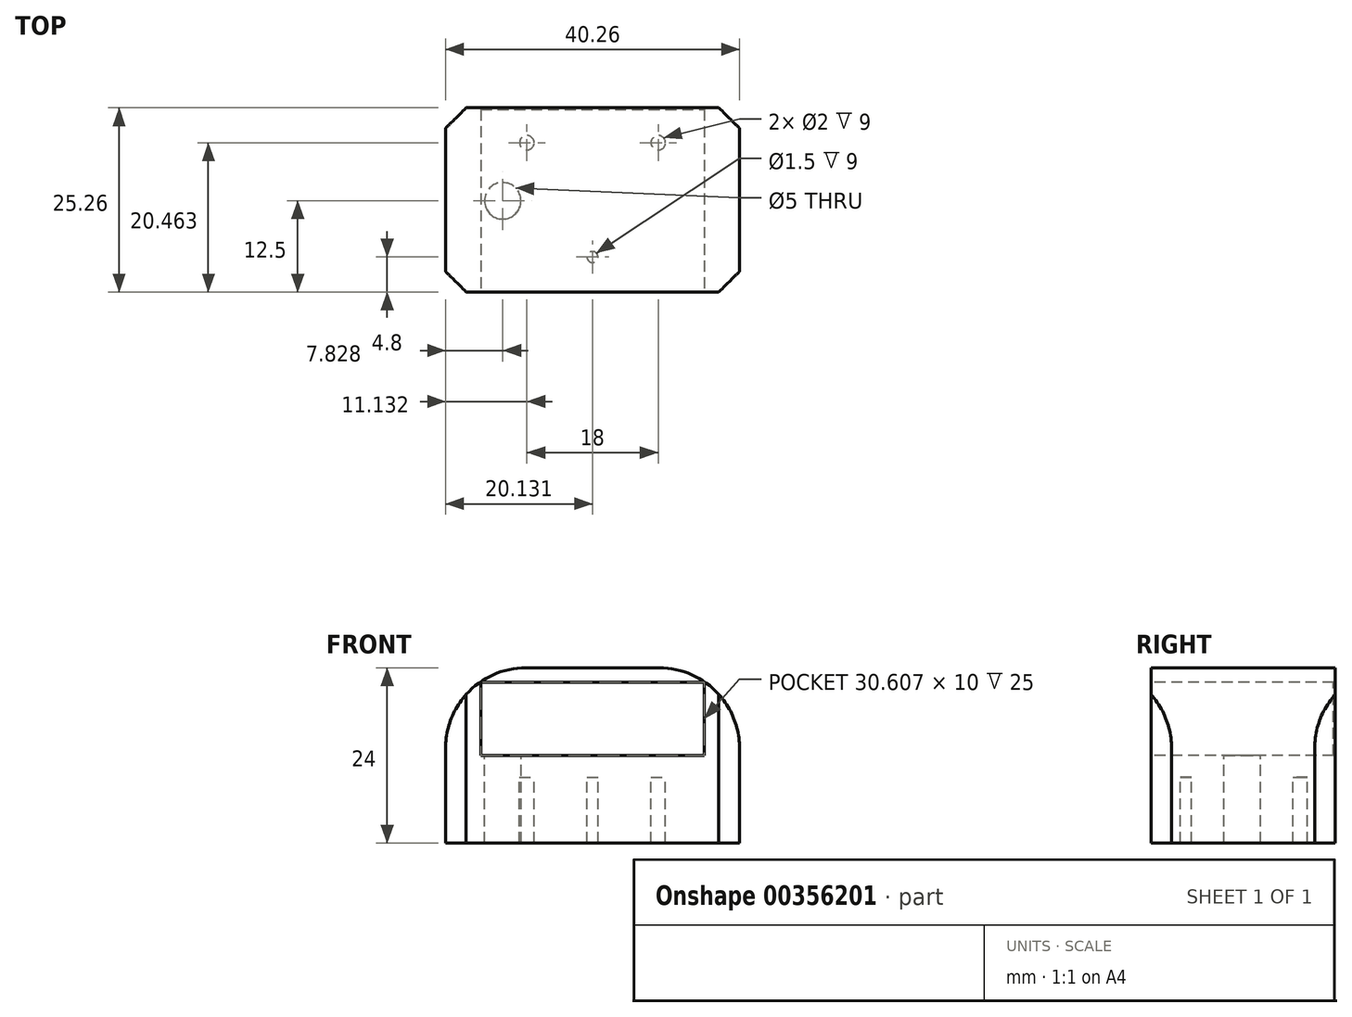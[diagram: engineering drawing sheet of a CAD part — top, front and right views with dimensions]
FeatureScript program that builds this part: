
annotation { "Feature Type Name" : "Feature", "Feature Type Description" : "" }
export const myFeature = defineFeature(function(context is Context, id is Id, definition is map)
    precondition{}
    {
        {
            var Q0;
            Q0=qCreatedBy(makeId("Top.planeOp"),FACE);
            var sketch = newSketch(context, id + "F0", { "sketchPlane" : qUnion([Q0])});
            skPoint(sketch, "E0", {"position": v(2.83, 25.26) * mm});
            skPoint(sketch, "E1", {"position": v(0, 22.43) * mm});
            skPoint(sketch, "E2", {"position": v(0, 2.83) * mm});
            skPoint(sketch, "E3", {"position": v(2.83, 0) * mm});
            skPoint(sketch, "E4", {"position": v(37.44, 0) * mm});
            skPoint(sketch, "E5", {"position": v(40.26, 2.83) * mm});
            skPoint(sketch, "E6", {"position": v(40.26, 22.43) * mm});
            skPoint(sketch, "E7", {"position": v(37.44, 25.26) * mm});
            skLineSegment(sketch, "E8", {"start": v(2.83, 25.26) * mm, "end": v(37.44, 25.26) * mm});
            skLineSegment(sketch, "E9", {"start": v(40.26, 22.43) * mm, "end": v(37.44, 25.26) * mm});
            skLineSegment(sketch, "E10", {"start": v(2.83, 25.26) * mm, "end": v(0, 22.43) * mm});
            skLineSegment(sketch, "E11", {"start": v(0, 22.43) * mm, "end": v(0, 2.83) * mm});
            skLineSegment(sketch, "E12", {"start": v(2.83, 0) * mm, "end": v(0, 2.83) * mm});
            skLineSegment(sketch, "E13", {"start": v(2.83, 0) * mm, "end": v(37.44, 0) * mm});
            skLineSegment(sketch, "E14", {"start": v(40.26, 2.83) * mm, "end": v(37.44, 0) * mm});
            skLineSegment(sketch, "E15", {"start": v(40.26, 2.83) * mm, "end": v(40.26, 22.43) * mm});
            skSolve(sketch);
        }
        {
            var Q0;
            Q0=qSketchRegion(id+"F0",true);
            extrude(context, id + "F1", {"entities" : qUnion([Q0]), "depth" : 15 * mm, "offsetDistance" : 25 * mm});
        }
        {
            var Q0;
            Q0=makeQuery(id+"F1.opExtrude","SWEPT_FACE",FACE,{"disambiguationData":[OSD([sQuery(id+"F0.wireOp",EDGE,"E13")])]});
            var sketch = newSketch(context, id + "F2", { "sketchPlane" : qUnion([Q0])});
            skPoint(sketch, "E16", {"position": v(4.83, 0) * mm});
            skPoint(sketch, "E17", {"position": v(2.83, 3) * mm});
            skPoint(sketch, "E18", {"position": v(35.44, 0) * mm});
            skPoint(sketch, "E19", {"position": v(37.44, 3) * mm});
            skLineSegment(sketch, "E20.bottom", {"start": v(4.83, 3) * mm, "end": v(35.44, 3) * mm});
            skLineSegment(sketch, "E20.top", {"start": v(4.83, 13) * mm, "end": v(35.44, 13) * mm});
            skLineSegment(sketch, "E20.left", {"start": v(4.83, 3) * mm, "end": v(4.83, 13) * mm});
            skLineSegment(sketch, "E20.right", {"start": v(35.44, 3) * mm, "end": v(35.44, 13) * mm});
            skSolve(sketch);
        }
        {
            var Q0;
            Q0=qSketchRegion(id+"F2",true);
            extrude(context, id + "F3", {"entities" : qUnion([Q0]), "operationType" : NewBodyOperationType.REMOVE, "oppositeDirection" : true, "depth" : 25 * mm});
        }
        {
            var Q0;
            Q0=qSketchRegion(id+"F2",true);
            extrude(context, id + "F4", {"entities" : qUnion([Q0]), "operationType" : NewBodyOperationType.REMOVE, "oppositeDirection" : true, "depth" : 20 * mm});
        }
        {
            var Q0;
            Q0=makeQuery(id+"F1.opExtrude","CAP_FACE",FACE,{"disambiguationData":[OSD([sQuery(id+"F0.wireOp",EDGE,"E8"),sQuery(id+"F0.wireOp",EDGE,"E9"),sQuery(id+"F0.wireOp",EDGE,"E10"),sQuery(id+"F0.wireOp",EDGE,"E11"),sQuery(id+"F0.wireOp",EDGE,"E12"),sQuery(id+"F0.wireOp",EDGE,"E13"),sQuery(id+"F0.wireOp",EDGE,"E14"),sQuery(id+"F0.wireOp",EDGE,"E15")])],"isStart":true});
            var sketch = newSketch(context, id + "F5", { "sketchPlane" : qUnion([Q0])});
            skPoint(sketch, "E21", {"position": v(0, -4.8) * mm});
            skPoint(sketch, "E22", {"position": v(0, -20.46) * mm});
            skPoint(sketch, "E23", {"position": v(40.26, -20.46) * mm});
            skPoint(sketch, "E24", {"position": v(40.26, -4.8) * mm});
            skLineSegment(sketch, "E25", {"start": v(40.26, -4.8) * mm, "end": v(0, -4.8) * mm});
            skLineSegment(sketch, "E26", {"start": v(0, -20.46) * mm, "end": v(40.26, -20.46) * mm});
            skCircle(sketch, "E27", {"center": v(20.13, -20.46) * mm, "radius": 1.5 * mm});
            skCircle(sketch, "E28", {"center": v(20.13, -4.8) * mm, "radius": 0.75 * mm});
            skPoint(sketch, "E29", {"position": v(11.13, -20.46) * mm});
            skPoint(sketch, "E30", {"position": v(29.13, -20.46) * mm});
            skCircle(sketch, "E31", {"center": v(29.13, -20.46) * mm, "radius": 1 * mm});
            skCircle(sketch, "E32", {"center": v(11.13, -20.46) * mm, "radius": 1 * mm});
            skPoint(sketch, "E33", {"position": v(29.13, -4.8) * mm});
            skSolve(sketch);
        }
        {
            var Q0;
            {var subQ0=sQuery(id+"F5.wireOp",EDGE,"Hm4tZGDY-VvXF-VA69-rOPO-ANf0YDS5IOW7");var subQ1=sQuery(id+"F5.wireOp",EDGE,"E25");var subQ2=makeQuery(id+"F5.imprint","INTERSECT",VERTEX,{"disambiguationData":[OD(0.0)],"derivedFrom":[subQ1,subQ0]});Q0=makeQuery(id+"F5.imprint","IMPRINT",FACE,{"disambiguationData":[TD([[makeQuery(id+"F5.imprint","IMPRINT",EDGE,{"disambiguationData":[TD([[subQ2,-1.0]])],"derivedFrom":subQ1}),-1.0]])]});}
            var Q1;
            {var subQ0=sQuery(id+"F5.wireOp",EDGE,"Hm4tZGDY-VvXF-VA69-rOPO-ANf0YDS5IOW7");var subQ1=sQuery(id+"F5.wireOp",EDGE,"E25");var subQ2=makeQuery(id+"F5.imprint","INTERSECT",VERTEX,{"disambiguationData":[OD(0.0)],"derivedFrom":[subQ1,subQ0]});Q1=makeQuery(id+"F5.imprint","IMPRINT",FACE,{"disambiguationData":[TD([[makeQuery(id+"F5.imprint","IMPRINT",EDGE,{"disambiguationData":[TD([[subQ2,-1.0]])],"derivedFrom":subQ1}),1.0]])]});}
            var Q2;
            {var subQ0=sQuery(id+"F5.wireOp",EDGE,"zMm4eNvp-IzTt-C4ok-0BIf-annPHVDxMdSz");var subQ1=sQuery(id+"F5.wireOp",EDGE,"E25");var subQ2=makeQuery(id+"F5.imprint","INTERSECT",VERTEX,{"disambiguationData":[OD(0.0)],"derivedFrom":[subQ1,subQ0]});Q2=makeQuery(id+"F5.imprint","IMPRINT",FACE,{"disambiguationData":[TD([[makeQuery(id+"F5.imprint","IMPRINT",EDGE,{"disambiguationData":[TD([[subQ2,-1.0]])],"derivedFrom":subQ1}),-1.0]])]});}
            var Q3;
            {var subQ0=sQuery(id+"F5.wireOp",EDGE,"zMm4eNvp-IzTt-C4ok-0BIf-annPHVDxMdSz");var subQ1=sQuery(id+"F5.wireOp",EDGE,"E25");var subQ2=makeQuery(id+"F5.imprint","INTERSECT",VERTEX,{"disambiguationData":[OD(0.0)],"derivedFrom":[subQ1,subQ0]});Q3=makeQuery(id+"F5.imprint","IMPRINT",FACE,{"disambiguationData":[TD([[makeQuery(id+"F5.imprint","IMPRINT",EDGE,{"disambiguationData":[TD([[subQ2,-1.0]])],"derivedFrom":subQ1}),1.0]])]});}
            var Q4;
            {var subQ0=sQuery(id+"F5.wireOp",EDGE,"E32");var subQ1=sQuery(id+"F5.wireOp",EDGE,"E26");var subQ2=makeQuery(id+"F5.imprint","INTERSECT",VERTEX,{"disambiguationData":[OD(0.0)],"derivedFrom":[subQ1,subQ0]});Q4=makeQuery(id+"F5.imprint","IMPRINT",FACE,{"disambiguationData":[TD([[makeQuery(id+"F5.imprint","IMPRINT",EDGE,{"disambiguationData":[TD([[subQ2,-1.0]])],"derivedFrom":subQ1}),1.0]])]});}
            var Q5;
            {var subQ0=sQuery(id+"F5.wireOp",EDGE,"E32");var subQ1=sQuery(id+"F5.wireOp",EDGE,"E26");var subQ2=makeQuery(id+"F5.imprint","INTERSECT",VERTEX,{"disambiguationData":[OD(0.0)],"derivedFrom":[subQ1,subQ0]});Q5=makeQuery(id+"F5.imprint","IMPRINT",FACE,{"disambiguationData":[TD([[makeQuery(id+"F5.imprint","IMPRINT",EDGE,{"disambiguationData":[TD([[subQ2,-1.0]])],"derivedFrom":subQ1}),-1.0]])]});}
            var Q6;
            {var subQ0=sQuery(id+"F5.wireOp",EDGE,"E27");var subQ1=sQuery(id+"F5.wireOp",EDGE,"E26");var subQ2=makeQuery(id+"F5.imprint","INTERSECT",VERTEX,{"disambiguationData":[OD(0.0)],"derivedFrom":[subQ1,subQ0]});Q6=makeQuery(id+"F5.imprint","IMPRINT",FACE,{"disambiguationData":[TD([[makeQuery(id+"F5.imprint","IMPRINT",EDGE,{"disambiguationData":[TD([[subQ2,-1.0]])],"derivedFrom":subQ1}),1.0]])]});}
            var Q7;
            {var subQ0=sQuery(id+"F5.wireOp",EDGE,"E27");var subQ1=sQuery(id+"F5.wireOp",EDGE,"E26");var subQ2=makeQuery(id+"F5.imprint","INTERSECT",VERTEX,{"disambiguationData":[OD(0.0)],"derivedFrom":[subQ1,subQ0]});Q7=makeQuery(id+"F5.imprint","IMPRINT",FACE,{"disambiguationData":[TD([[makeQuery(id+"F5.imprint","IMPRINT",EDGE,{"disambiguationData":[TD([[subQ2,-1.0]])],"derivedFrom":subQ1}),-1.0]])]});}
            var Q8;
            {var subQ0=sQuery(id+"F5.wireOp",EDGE,"E31");var subQ1=sQuery(id+"F5.wireOp",EDGE,"E26");var subQ2=makeQuery(id+"F5.imprint","INTERSECT",VERTEX,{"disambiguationData":[OD(0.0)],"derivedFrom":[subQ1,subQ0]});Q8=makeQuery(id+"F5.imprint","IMPRINT",FACE,{"disambiguationData":[TD([[makeQuery(id+"F5.imprint","IMPRINT",EDGE,{"disambiguationData":[TD([[subQ2,-1.0]])],"derivedFrom":subQ1}),-1.0]])]});}
            var Q9;
            {var subQ0=sQuery(id+"F5.wireOp",EDGE,"E31");var subQ1=sQuery(id+"F5.wireOp",EDGE,"E26");var subQ2=makeQuery(id+"F5.imprint","INTERSECT",VERTEX,{"disambiguationData":[OD(0.0)],"derivedFrom":[subQ1,subQ0]});Q9=makeQuery(id+"F5.imprint","IMPRINT",FACE,{"disambiguationData":[TD([[makeQuery(id+"F5.imprint","IMPRINT",EDGE,{"disambiguationData":[TD([[subQ2,-1.0]])],"derivedFrom":subQ1}),1.0]])]});}
            extrude(context, id + "F6", {"entities" : qUnion([Q0, Q1, Q2, Q3, Q4, Q5, Q6, Q7, Q8, Q9]), "operationType" : NewBodyOperationType.ADD, "depth" : 9 * mm, "offsetDistance" : 25 * mm});
        }
        {
            var Q0;
            {var subQ0=sQuery(id+"F5.wireOp",EDGE,"E28");var subQ1=sQuery(id+"F5.wireOp",EDGE,"E25");var subQ2=makeQuery(id+"F5.imprint","INTERSECT",VERTEX,{"disambiguationData":[OD(0.0)],"derivedFrom":[subQ1,subQ0]});Q0=makeQuery(id+"F5.imprint","IMPRINT",FACE,{"disambiguationData":[TD([[makeQuery(id+"F5.imprint","IMPRINT",EDGE,{"disambiguationData":[TD([[subQ2,-1.0]])],"derivedFrom":subQ1}),-1.0]])]});}
            var Q1;
            {var subQ0=sQuery(id+"F5.wireOp",EDGE,"E28");var subQ1=sQuery(id+"F5.wireOp",EDGE,"E25");var subQ2=makeQuery(id+"F5.imprint","INTERSECT",VERTEX,{"disambiguationData":[OD(0.0)],"derivedFrom":[subQ1,subQ0]});Q1=makeQuery(id+"F5.imprint","IMPRINT",FACE,{"disambiguationData":[TD([[makeQuery(id+"F5.imprint","IMPRINT",EDGE,{"disambiguationData":[TD([[subQ2,-1.0]])],"derivedFrom":subQ1}),1.0]])]});}
            extrude(context, id + "F7", {"entities" : qUnion([Q0, Q1]), "operationType" : NewBodyOperationType.ADD, "depth" : 9 * mm, "offsetDistance" : 25 * mm});
        }
        {
            var Q0;
            Q0=makeQuery(id+"F1.opExtrude","CAP_EDGE",EDGE,{"disambiguationData":[OSD([sQuery(id+"F0.wireOp",EDGE,"E15")])],"isStart":false});
            var Q1;
            Q1=makeQuery(id+"F1.opExtrude","CAP_EDGE",EDGE,{"disambiguationData":[OSD([sQuery(id+"F0.wireOp",EDGE,"E11")])],"isStart":false});
            fillet(context, id + "F8", {"entities" : qUnion([Q0, Q1]), "radius" : 11 * mm, "tangentPropagation" : true, "allowEdgeOverflow" : false});
        }
        {
            var Q0;
            Q0=makeQuery(id+"F3.boolean.opBoolean","COPY",FACE,{"derivedFrom":makeQuery(id+"F3.opExtrude","SWEPT_FACE",FACE,{"disambiguationData":[OSD([sQuery(id+"F2.wireOp",EDGE,"E20.bottom")])]})});
            var sketch = newSketch(context, id + "F9", { "sketchPlane" : qUnion([Q0])});
            skPoint(sketch, "E34", {"position": v(4.83, 12.5) * mm});
            skPoint(sketch, "E35", {"position": v(7.83, 25) * mm});
            skCircle(sketch, "E36", {"center": v(7.83, 12.5) * mm, "radius": 2.5 * mm});
            skSolve(sketch);
        }
        {
            var Q0;
            Q0 = qSketchRegion(id + "F9", true);
            extrude(context, id + "F10", {"entities" : qUnion([Q0]), "operationType" : NewBodyOperationType.REMOVE, "oppositeDirection" : true, "depth" : 25 * mm, "offsetDistance" : 25 * mm});
        }
    });
